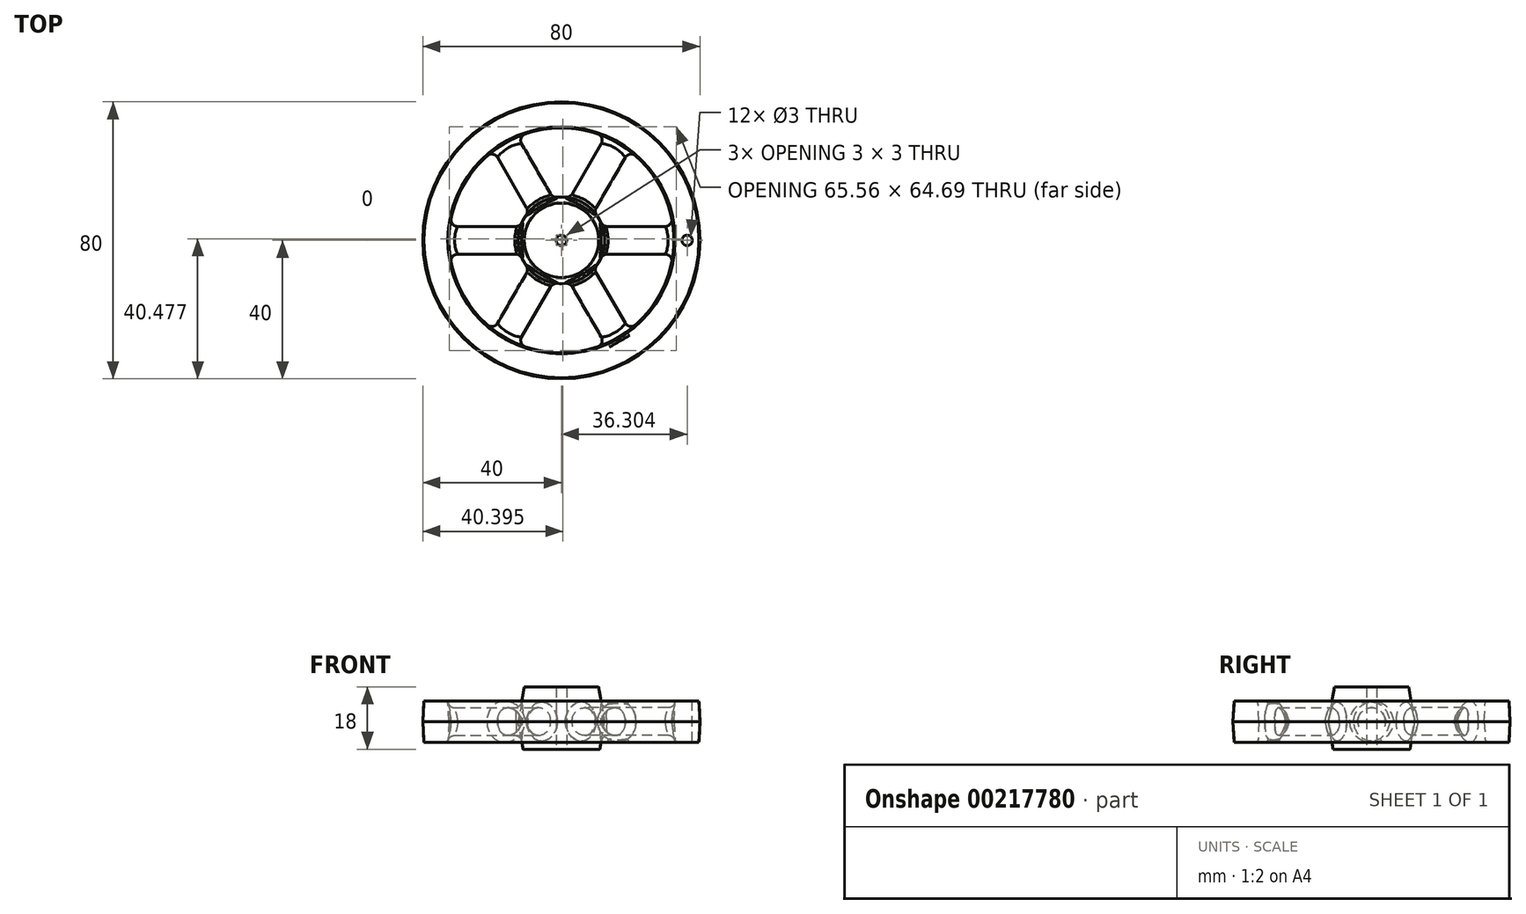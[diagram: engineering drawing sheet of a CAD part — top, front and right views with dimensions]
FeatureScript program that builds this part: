
annotation { "Feature Type Name" : "Feature", "Feature Type Description" : "" }
export const myFeature = defineFeature(function(context is Context, id is Id, definition is map)
    precondition{}
    {
        {
            var Q0;
            Q0=qCreatedBy(makeId("Top.planeOp"),FACE);
            var sketch = newSketch(context, id + "F0", { "sketchPlane" : qUnion([Q0])});
            skCircle(sketch, "E0", {"center": v(0, 0) * mm, "radius": 32.5 * mm});
            skCircle(sketch, "E1", {"center": v(0, 0) * mm, "radius": 40 * mm});
            skSolve(sketch);
        }
        {
            var Q0;
            Q0 = qSketchRegion(id + "F0", true);
            extrude(context, id + "F1", {"entities" : qUnion([Q0]), "depth" : 6 * mm, "hasDraft" : true, "draftAngle" : 3 * degree, "draftPullDirection" : true, "hasSecondDirection" : true, "secondDirectionOppositeDirection" : true, "secondDirectionDepth" : 6 * mm, "hasSecondDirectionDraft" : true, "secondDirectionDraftAngle" : 3 * degree, "secondDirectionDraftPullDirection" : true});
        }
        {
            var Q0;
            Q0=qCreatedBy(makeId("Top.planeOp"),FACE);
            var sketch = newSketch(context, id + "F2", { "sketchPlane" : qUnion([Q0])});
            skCircle(sketch, "E2", {"center": v(0, 0) * mm, "radius": 12.5 * mm});
            skSolve(sketch);
        }
        {
            var Q0;
            Q0 = qSketchRegion(id + "F2", true);
            extrude(context, id + "F3", {"entities" : qUnion([Q0]), "depth" : 10 * mm, "hasDraft" : true, "draftAngle" : 10 * degree, "draftPullDirection" : true, "hasSecondDirection" : true, "secondDirectionOppositeDirection" : true, "secondDirectionDepth" : 8 * mm, "hasSecondDirectionDraft" : true, "secondDirectionDraftAngle" : 10 * degree, "secondDirectionDraftPullDirection" : true});
        }
        {
            var Q0;
            Q0=qCreatedBy(makeId("Right.planeOp"),FACE);
            var sketch = newSketch(context, id + "F4", { "sketchPlane" : qUnion([Q0])});
            skCircle(sketch, "E3", {"center": v(0, 0) * mm, "radius": 4 * mm});
            skSolve(sketch);
        }
        {
            var Q0;
            Q0 = qSketchRegion(id + "F4", true);
            extrude(context, id + "F5", {"entities" : qUnion([Q0]), "operationType" : NewBodyOperationType.ADD, "depth" : 35 * mm});
        }
        {
            var Q0;
            Q0=makeQuery(id+"F5.opExtrude","SWEPT_FACE",FACE,{"disambiguationData":[OSD([sQuery(id+"F4.wireOp",EDGE,"E3")])]});
            fillet(context, id + "F6", {"entities" : qUnion([Q0]), "radius" : 2 * mm, "tangentPropagation" : true, "allowEdgeOverflow" : false});
        }
        {
            var Q0;
            Q0=makeQuery(id+"F1.opExtrude","SWEPT_BODY",BODY,{"disambiguationData":[OSD([sQuery(id+"F0.wireOp",EDGE,"E0"),sQuery(id+"F0.wireOp",EDGE,"E1")])]});
            var Q1;
            Q1=sQuery(id+"F0.wireOp",EDGE,"E1");
            circularPattern(context, id + "F7", {"entities" : qUnion([Q0]), "axis" : qUnion([Q1]), "angle" : 360 * degree, "instanceCount" : 6, "equalSpace" : true});
        }
        {
            var Q0;
            Q0=makeQuery(id+"F3.opExtrude","CAP_FACE",FACE,{"disambiguationData":[OSD([sQuery(id+"F2.wireOp",EDGE,"E2")])],"isStart":true});
            var sketch = newSketch(context, id + "F8", { "sketchPlane" : qUnion([Q0])});
            skPoint(sketch, "E4", {"position": v(0, 0) * mm});
            skSolve(sketch);
        }
        {
            var Q0;
            Q0=sQuery(id+"F8.wireOp",VERTEX,"E4");
            var Q1;
            Q1=makeQuery(id+"F1.split0.splitOp","SPLIT",BODY,{"derivedFrom":makeQuery(id+"F1.opExtrude","SWEPT_BODY",BODY,{"disambiguationData":[OSD([sQuery(id+"F0.wireOp",EDGE,"E0"),sQuery(id+"F0.wireOp",EDGE,"E1")])]})});
            var Q2;
            Q2=makeQuery(id+"F7.opPattern","COPY",BODY,{"derivedFrom":makeQuery(id+"F1.split0.splitOp","SPLIT",BODY,{"derivedFrom":makeQuery(id+"F1.opExtrude","SWEPT_BODY",BODY,{"disambiguationData":[OSD([sQuery(id+"F0.wireOp",EDGE,"E0"),sQuery(id+"F0.wireOp",EDGE,"E1")])]})}),"instanceName":"2"});
            var Q3;
            Q3=makeQuery(id+"F7.opPattern","COPY",BODY,{"derivedFrom":makeQuery(id+"F1.split0.splitOp","SPLIT",BODY,{"derivedFrom":makeQuery(id+"F1.opExtrude","SWEPT_BODY",BODY,{"disambiguationData":[OSD([sQuery(id+"F0.wireOp",EDGE,"E0"),sQuery(id+"F0.wireOp",EDGE,"E1")])]})}),"instanceName":"1"});
            var Q4;
            Q4=makeQuery(id+"F7.opPattern","COPY",BODY,{"derivedFrom":makeQuery(id+"F1.split0.splitOp","SPLIT",BODY,{"derivedFrom":makeQuery(id+"F1.opExtrude","SWEPT_BODY",BODY,{"disambiguationData":[OSD([sQuery(id+"F0.wireOp",EDGE,"E0"),sQuery(id+"F0.wireOp",EDGE,"E1")])]})}),"instanceName":"3"});
            var Q5;
            Q5=makeQuery(id+"F7.opPattern","COPY",BODY,{"derivedFrom":makeQuery(id+"F1.split0.splitOp","SPLIT",BODY,{"derivedFrom":makeQuery(id+"F1.opExtrude","SWEPT_BODY",BODY,{"disambiguationData":[OSD([sQuery(id+"F0.wireOp",EDGE,"E0"),sQuery(id+"F0.wireOp",EDGE,"E1")])]})}),"instanceName":"4"});
            var Q6;
            Q6=makeQuery(id+"F7.opPattern","COPY",BODY,{"derivedFrom":makeQuery(id+"F1.split0.splitOp","SPLIT",BODY,{"derivedFrom":makeQuery(id+"F1.opExtrude","SWEPT_BODY",BODY,{"disambiguationData":[OSD([sQuery(id+"F0.wireOp",EDGE,"E0"),sQuery(id+"F0.wireOp",EDGE,"E1")])]})}),"instanceName":"5"});
            hole(context, id + "F9", {"style" : HoleStyle.SIMPLE, "endStyle" : HoleEndStyle.THROUGH, "holeDiameter" : 3 * mm, "locations" : qUnion([Q0]), "scope" : qUnion([Q1, Q2, Q3, Q4, Q5, Q6]), "isTappedThrough" : true});
        }
        {
            var Q0;
            Q0=makeQuery(id+"F1.opExtrude","CAP_FACE",FACE,{"disambiguationData":[OSD([sQuery(id+"F0.wireOp",EDGE,"E0"),sQuery(id+"F0.wireOp",EDGE,"E1")])],"isStart":false});
            var sketch = newSketch(context, id + "F10", { "sketchPlane" : qUnion([Q0])});
            skLineSegment(sketch, "E5", {"start": v(0, 0) * mm, "end": v(37.19, 0) * mm, "construction": true});
            skPoint(sketch, "E6", {"position": v(36.3, 0) * mm});
            skLineSegment(sketch, "E7", {"start": v(37.19, 0) * mm, "end": v(39.69, 0) * mm, "construction": true});
            skSolve(sketch);
        }
        {
            var Q0;
            Q0=sQuery(id+"F10.wireOp",VERTEX,"E6");
            var Q1;
            Q1=makeQuery(id+"F1.split0.splitOp","SPLIT",BODY,{"derivedFrom":makeQuery(id+"F1.opExtrude","SWEPT_BODY",BODY,{"disambiguationData":[OSD([sQuery(id+"F0.wireOp",EDGE,"E0"),sQuery(id+"F0.wireOp",EDGE,"E1")])]})});
            var Q2;
            Q2=makeQuery(id+"F7.opPattern","COPY",BODY,{"derivedFrom":makeQuery(id+"F1.split0.splitOp","SPLIT",BODY,{"derivedFrom":makeQuery(id+"F1.opExtrude","SWEPT_BODY",BODY,{"disambiguationData":[OSD([sQuery(id+"F0.wireOp",EDGE,"E0"),sQuery(id+"F0.wireOp",EDGE,"E1")])]})}),"instanceName":"1"});
            var Q3;
            Q3=makeQuery(id+"F7.opPattern","COPY",BODY,{"derivedFrom":makeQuery(id+"F1.split0.splitOp","SPLIT",BODY,{"derivedFrom":makeQuery(id+"F1.opExtrude","SWEPT_BODY",BODY,{"disambiguationData":[OSD([sQuery(id+"F0.wireOp",EDGE,"E0"),sQuery(id+"F0.wireOp",EDGE,"E1")])]})}),"instanceName":"2"});
            var Q4;
            Q4=makeQuery(id+"F7.opPattern","COPY",BODY,{"derivedFrom":makeQuery(id+"F1.split0.splitOp","SPLIT",BODY,{"derivedFrom":makeQuery(id+"F1.opExtrude","SWEPT_BODY",BODY,{"disambiguationData":[OSD([sQuery(id+"F0.wireOp",EDGE,"E0"),sQuery(id+"F0.wireOp",EDGE,"E1")])]})}),"instanceName":"3"});
            var Q5;
            Q5=makeQuery(id+"F7.opPattern","COPY",BODY,{"derivedFrom":makeQuery(id+"F1.split0.splitOp","SPLIT",BODY,{"derivedFrom":makeQuery(id+"F1.opExtrude","SWEPT_BODY",BODY,{"disambiguationData":[OSD([sQuery(id+"F0.wireOp",EDGE,"E0"),sQuery(id+"F0.wireOp",EDGE,"E1")])]})}),"instanceName":"4"});
            var Q6;
            Q6=makeQuery(id+"F7.opPattern","COPY",BODY,{"derivedFrom":makeQuery(id+"F1.split0.splitOp","SPLIT",BODY,{"derivedFrom":makeQuery(id+"F1.opExtrude","SWEPT_BODY",BODY,{"disambiguationData":[OSD([sQuery(id+"F0.wireOp",EDGE,"E0"),sQuery(id+"F0.wireOp",EDGE,"E1")])]})}),"instanceName":"5"});
            hole(context, id + "F11", {"style" : HoleStyle.SIMPLE, "endStyle" : HoleEndStyle.THROUGH, "holeDiameter" : 3 * mm, "locations" : qUnion([Q0]), "scope" : qUnion([Q1, Q2, Q3, Q4, Q5, Q6]), "isTappedThrough" : true});
        }
        {
            var Q0;
            Q0=makeQuery(id+"F7.opPattern","COPY",EDGE,{"derivedFrom":makeQuery(id+"F3.opExtrude","CAP_EDGE",EDGE,{"disambiguationData":[OSD([sQuery(id+"F2.wireOp",EDGE,"E2")])],"isStart":true}),"instanceName":"5"});
            var Q1;
            Q1=makeQuery(id+"F7.opPattern","COPY",EDGE,{"derivedFrom":makeQuery(id+"F1.opExtrude","CAP_EDGE",EDGE,{"disambiguationData":[OSD([sQuery(id+"F0.wireOp",EDGE,"E0")])],"isStart":true}),"instanceName":"5"});
            var Q2;
            Q2=makeQuery(id+"F7.opPattern","COPY",EDGE,{"derivedFrom":makeQuery(id+"F1.opExtrude","CAP_EDGE",EDGE,{"disambiguationData":[OSD([sQuery(id+"F0.wireOp",EDGE,"E1")])],"isStart":true}),"instanceName":"5"});
            var Q3;
            Q3=makeQuery(id+"F7.opPattern","COPY",EDGE,{"derivedFrom":makeQuery(id+"F3.opExtrude","CAP_EDGE",EDGE,{"disambiguationData":[OSD([sQuery(id+"F2.wireOp",EDGE,"E2")])],"isStart":false}),"instanceName":"5"});
            var Q4;
            Q4=makeQuery(id+"F7.opPattern","COPY",EDGE,{"derivedFrom":makeQuery(id+"F1.opExtrude","CAP_EDGE",EDGE,{"disambiguationData":[OSD([sQuery(id+"F0.wireOp",EDGE,"E0")])],"isStart":false}),"instanceName":"5"});
            var Q5;
            Q5=makeQuery(id+"F7.opPattern","COPY",EDGE,{"derivedFrom":makeQuery(id+"F1.opExtrude","CAP_EDGE",EDGE,{"disambiguationData":[OSD([sQuery(id+"F0.wireOp",EDGE,"E1")])],"isStart":false}),"instanceName":"5"});
            fillet(context, id + "F12", {"entities" : qUnion([Q0, Q1, Q2, Q3, Q4, Q5]), "radius" : 1 * mm, "tangentPropagation" : true, "allowEdgeOverflow" : false});
        }
    });
